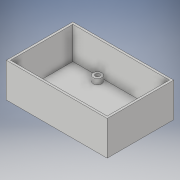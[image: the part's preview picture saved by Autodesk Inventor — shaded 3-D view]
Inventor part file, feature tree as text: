
AUTODESK INVENTOR PART (.ipt)
format: ipt  version: 2019.4 (Build 234330000, 330)  size: 129,024 bytes
history: native  units: mm
features: extrude x3, sketch x3
ambient origin geometry x8: Origin, YZ Plane, XZ Plane, XY Plane, X Axis, Y Axis, Z Axis, Center Point
bodies: Solid1 (feature_tree)
feature tree (6):
  extrude  "Extrusion1"  Depth=58.0mm
  extrude  "Extrusion2"  Depth=32.0mm TaperAngle=0.0deg
  extrude  "Extrusion3"  Depth=58.0mm
  sketch  "Sketch1"  dims[d0=90.0mm d1=58.0mm]
  sketch  "Sketch2"  dims[d2=2.0mm d3=32.0mm d4=0.0mm]
  sketch  "Sketch3"  dims[d5=90.0mm d6=58.0mm d7=30.0mm d8=0.0mm d9=4.5mm d10=4.5mm d11=4.0mm d12=8.0mm d13=20.0mm d15=49.0mm d16=20.0mm d18=58.0mm d21=5.0mm d22=0.0mm]
